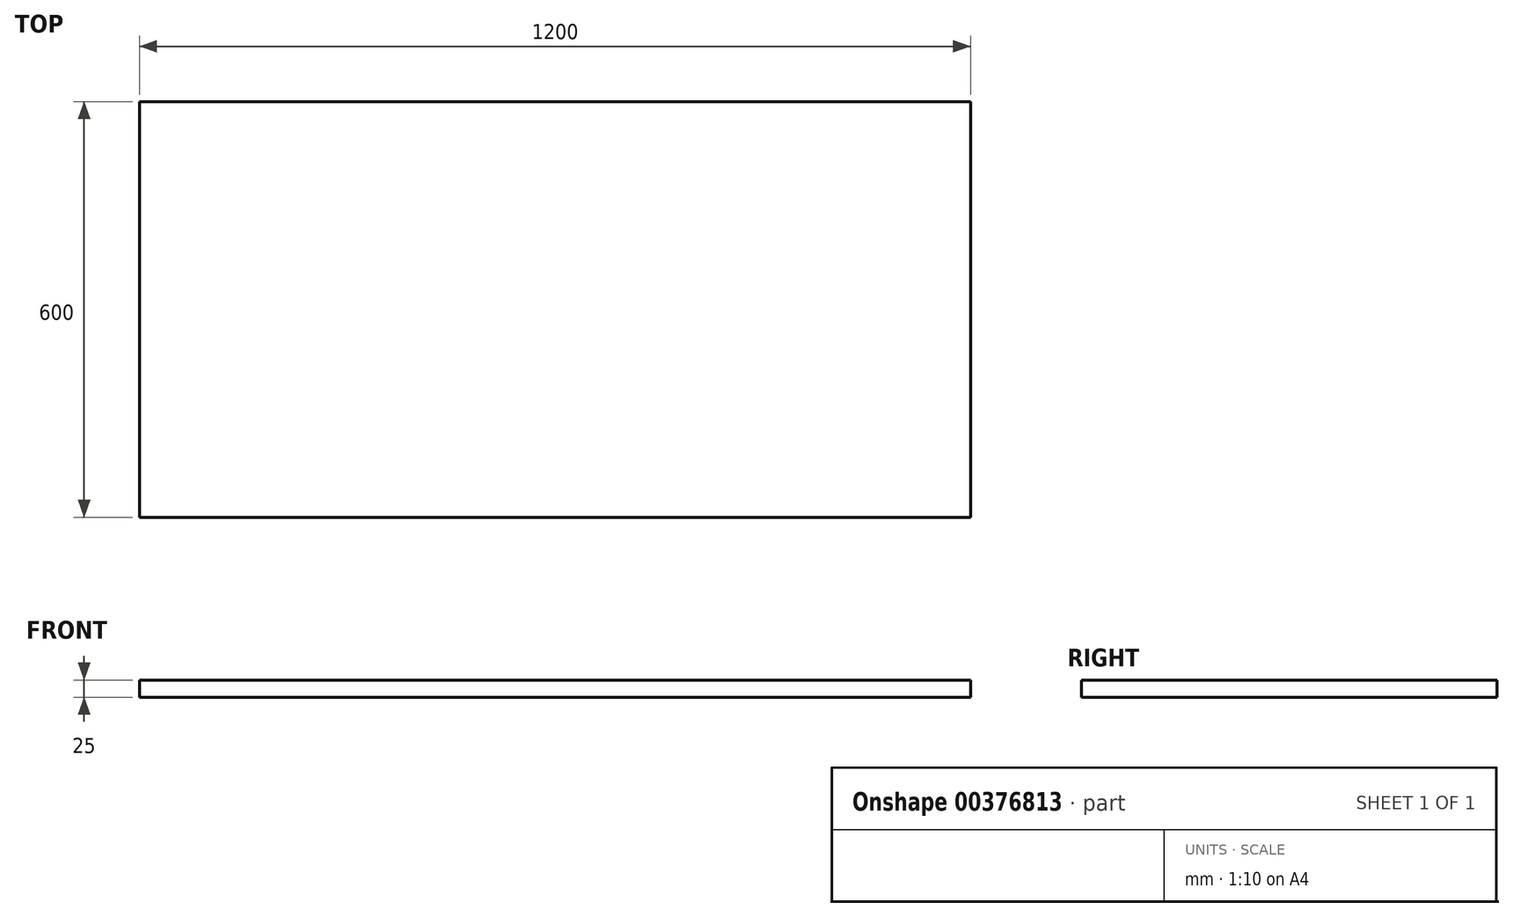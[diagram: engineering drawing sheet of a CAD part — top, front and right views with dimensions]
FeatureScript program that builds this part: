
annotation { "Feature Type Name" : "Feature", "Feature Type Description" : "" }
export const myFeature = defineFeature(function(context is Context, id is Id, definition is map)
    precondition{}
    {
        {
            var Q0;
            Q0=qCreatedBy(makeId("Top.planeOp"),FACE);
            var sketch = newSketch(context, id + "F0", { "sketchPlane" : qUnion([Q0])});
            skLineSegment(sketch, "E0.bottom", {"start": v(535.93, -262.53) * mm, "end": v(-664.07, -262.53) * mm});
            skLineSegment(sketch, "E0.top", {"start": v(535.93, 337.47) * mm, "end": v(-664.07, 337.47) * mm});
            skLineSegment(sketch, "E0.left", {"start": v(535.93, -262.53) * mm, "end": v(535.93, 337.47) * mm});
            skLineSegment(sketch, "E0.right", {"start": v(-664.07, -262.53) * mm, "end": v(-664.07, 337.47) * mm});
            skPoint(sketch, "E0.middle", {"position": v(-64.07, 37.47) * mm});
            skSolve(sketch);
        }
        {
            var Q0;
            Q0=qSketchRegion(id+"F0",true);
            extrude(context, id + "F1", {"entities" : qUnion([Q0]), "depth" : 25 * mm});
        }
    });
